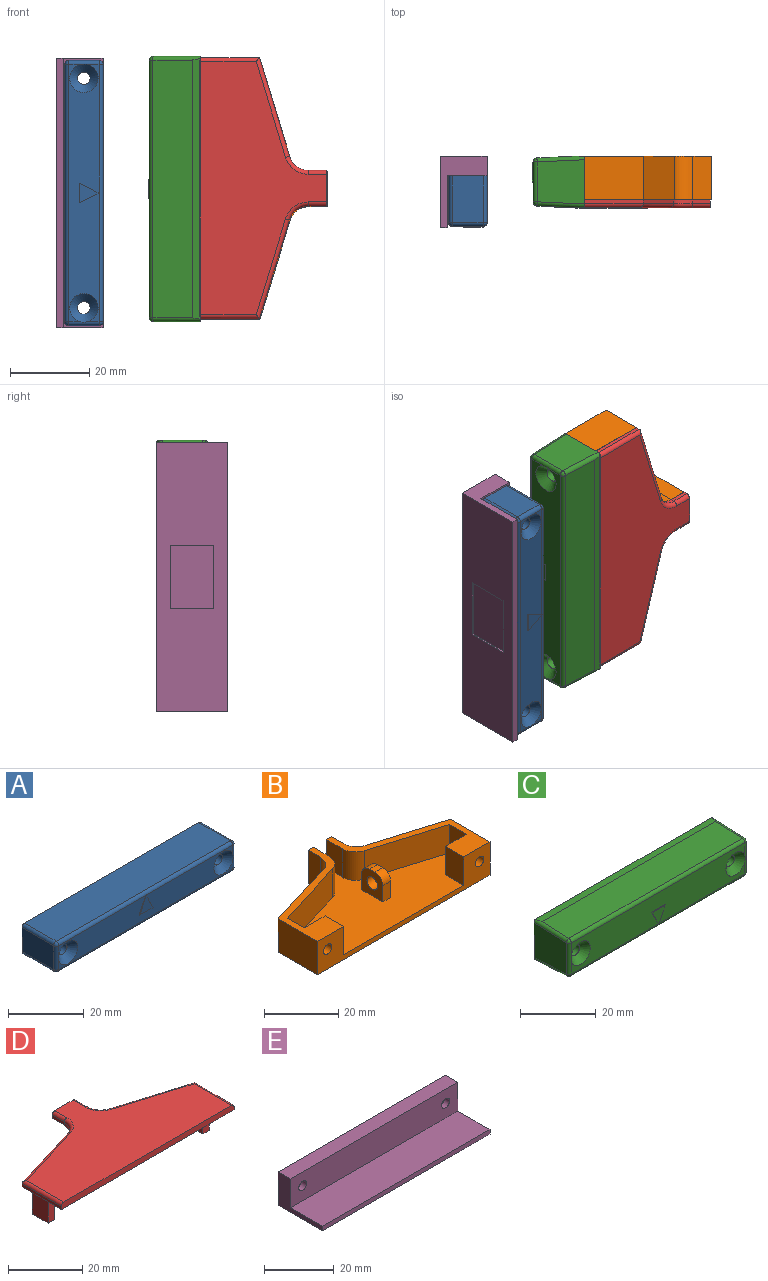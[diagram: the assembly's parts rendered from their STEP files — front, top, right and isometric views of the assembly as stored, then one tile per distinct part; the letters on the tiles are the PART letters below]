
ASSEMBLY  parts=5 mates=4
PART A: 26 faces, bbox 67x12.9x9.7 mm
  f0: plane 65x11.7mm, normal (0,0,1), area 760.5mm2, adj f5,f16,f22,f25
  f1: plane 11.7x7.7mm, normal (-1,0,0), area 90.1mm2, adj f5,f19,f23,f25
  f2: plane 65x11.7mm, normal (0,0,-1), area 760.5mm2, adj f5,f14,f18,f19
  f3: plane 11.7x7.7mm, normal (1,0,0), area 90.1mm2, adj f5,f14,f16,f17
  f4: plane 65x7.7mm, normal (0,-1,0), area 406.8mm2, adj f6,f7,f8,f12,f13,f17,f18,f22
  f5: plane 67x9.7mm, normal (0,1,0), area 633mm2, adj f0,f1,f2,f3,f10,f11,f14,f16
  f6: plane 5x2.5mm, normal (0.89,0,0.45), area 1.1mm2, adj f4,f7,f8,f9
  f7: plane 5x2.5mm, normal (-0.89,0,0.45), area 1.1mm2, adj f4,f6,f8,f9
  f8: plane 5x0.2mm, normal (0,0,-1), area 1mm2, adj f4,f6,f7,f9
  f9: plane 5x5mm, normal (0,-1,0), area 12.5mm2, adj f6,f7,f8
  f10: cylinder r=1.6mm len=10.7mm, axis (0,-1,0), area 107.6mm2, adj f5,f12
  f11: cylinder r=1.6mm len=10.7mm, axis (0,-1,0), area 107.6mm2, adj f5,f13
  f12: cone r=1.6mm half-angle=45deg, axis (0,-1,0), area 46.2mm2, adj f4,f10,f23
  f13: cone r=1.6mm half-angle=45deg, axis (0,-1,0), area 46.2mm2, adj f4,f11,f17
  f14: cylinder r=1mm len=11.7mm, axis (0,-1,0), area 18.4mm2, adj f2,f3,f5,f15
  f15: sphere r=1mm, area 1.6mm2, adj f14,f17,f18
  f16: cylinder r=1mm len=11.7mm, axis (0,1,0), area 18.4mm2, adj f0,f3,f5,f20
  f17: cylinder r=1mm len=7.7mm, axis (0,0,-1), area 12mm2, adj f3,f4,f13,f15,f20
  f18: cylinder r=1mm len=65mm, axis (-1,0,0), area 102.1mm2, adj f2,f4,f15,f21
  f19: cylinder r=1mm len=11.7mm, axis (0,1,0), area 18.4mm2, adj f1,f2,f5,f21
  f20: sphere r=1mm, area 1.6mm2, adj f16,f17,f22
  f21: sphere r=1mm, area 1.6mm2, adj f18,f19,f23
  f22: cylinder r=1mm len=65mm, axis (1,0,0), area 102.1mm2, adj f0,f4,f20,f24
  f23: cylinder r=1mm len=7.7mm, axis (0,0,1), area 12mm2, adj f1,f4,f12,f21,f24
  f24: sphere r=1mm, area 1.6mm2, adj f22,f23,f25
  f25: cylinder r=1mm len=11.7mm, axis (0,-1,0), area 18.4mm2, adj f0,f1,f5,f24
PART B: 57 faces, bbox 66x32x11 mm
  f0: plane 66x32mm, normal (0,0,-1), area 995.4mm2, adj f3,f4,f5,f6,f7,f8,f9,f10
  f1: plane 62x32mm, normal (0,0,1), area 1046.9mm2, adj f2,f4,f8,f11,f12,f14,f32,f33
  f2: plane 9.4x8mm, normal (0,1,0), area 48.1mm2, adj f1,f14,f15,f26,f27,f28,f29,f31
  f3: plane 15x11mm, normal (1,0,0), area 165mm2, adj f0,f4,f10,f15
  f4: plane 66x11mm, normal (0,-1,0), area 277.5mm2, adj f0,f1,f3,f5,f12,f13,f14,f15
  f5: plane 15x11mm, normal (-1,0,0), area 165mm2, adj f0,f4,f6,f13
  f6: plane 24.96x11mm, normal (-0.29,0.96,0), area 286.9mm2, adj f0,f5,f13,f50
  f7: plane 11x4.62mm, normal (-1,0,0), area 50.8mm2, adj f0,f8,f13,f50
  f8: plane 11x9mm, normal (0,1,0), area 52mm2, adj f0,f1,f7,f9,f13,f15,f34,f39
  f9: plane 11x4.62mm, normal (1,0,0), area 50.8mm2, adj f0,f8,f15,f51
  f10: plane 24.96x11mm, normal (0.29,0.96,0), area 286.9mm2, adj f0,f3,f15,f51
  f11: plane 9.4x8mm, normal (0,1,0), area 48.1mm2, adj f1,f12,f13,f19,f20,f21,f22,f23
  f12: plane 9.4x7mm, normal (1,0,0), area 65.8mm2, adj f1,f4,f11,f13
  f13: plane 32x30.5mm, normal (0,0,1), area 162.2mm2, adj f4,f5,f6,f7,f8,f11,f12,f32
  f14: plane 9.4x7mm, normal (-1,0,0), area 65.8mm2, adj f1,f2,f4,f15
  f15: plane 32x30.5mm, normal (0,0,1), area 162.2mm2, adj f2,f3,f4,f8,f9,f10,f14,f36
  f16: cylinder r=1.6mm len=3.2mm, axis (0,-1,0), area 30.2mm2, adj f4,f25
  f17: cylinder r=1.6mm len=3.2mm, axis (0,-1,0), area 30.2mm2, adj f4,f18
  f18: plane 6.93x6mm, normal (0,1,0), area 23.1mm2, adj f17,f19,f20,f21,f22,f23,f24
  f19: plane 4x3mm, normal (-0.5,0,-0.87), area 13.9mm2, adj f11,f18,f20,f22
  f20: plane 4x3.46mm, normal (-1,0,0), area 13.9mm2, adj f11,f18,f19,f21
  f21: plane 4x3mm, normal (-0.5,0,0.87), area 13.9mm2, adj f11,f18,f20,f23
  f22: plane 4x3mm, normal (0.5,0,-0.87), area 13.9mm2, adj f11,f18,f19,f24,f35
  f23: plane 4x3mm, normal (0.5,0,0.87), area 13.9mm2, adj f11,f18,f21,f24,f35
  f24: plane 4x3.46mm, normal (1,0,0), area 13.9mm2, adj f18,f22,f23,f35
  f25: plane 6.93x6mm, normal (0,1,0), area 23.1mm2, adj f16,f26,f27,f28,f29,f30,f31
  f26: plane 4x3mm, normal (0.5,0,0.87), area 13.9mm2, adj f2,f25,f27,f31
  f27: plane 4x3.46mm, normal (1,0,0), area 13.9mm2, adj f2,f25,f26,f28
  f28: plane 4x3mm, normal (0.5,0,-0.87), area 13.9mm2, adj f2,f25,f27,f29
  f29: plane 4x3mm, normal (-0.5,0,-0.87), area 13.9mm2, adj f2,f25,f28,f30,f38
  f30: plane 4x3.46mm, normal (-1,0,0), area 13.9mm2, adj f25,f29,f31,f38
  f31: plane 4x3mm, normal (-0.5,0,0.87), area 13.9mm2, adj f2,f25,f26,f30,f38
  f32: plane 9.4x6.52mm, normal (1,0,0), area 61.3mm2, adj f1,f11,f13,f33,f35
  f33: plane 24.96x9.4mm, normal (0.29,-0.96,0), area 245.2mm2, adj f1,f13,f32,f49
  f34: plane 9.4x6.1mm, normal (1,0,0), area 57.4mm2, adj f1,f8,f13,f49
  f35: plane 4.62x1mm, normal (0,-1,0), area 4mm2, adj f22,f23,f24,f32
  f36: plane 24.96x9.4mm, normal (-0.29,-0.96,0), area 245.2mm2, adj f1,f15,f37,f48
  f37: plane 9.4x6.52mm, normal (-1,0,0), area 61.3mm2, adj f1,f2,f15,f36,f38
  f38: plane 4.62x1mm, normal (0,-1,0), area 4mm2, adj f29,f30,f31,f37
  f39: plane 9.4x6.1mm, normal (-1,0,0), area 57.4mm2, adj f1,f8,f15,f48
  f40: plane 3x2mm, normal (0,0,1), area 6mm2, adj f41,f44,f46,f47
  f41: plane 8.4x8mm, normal (-1,0,0), area 50.8mm2, adj f1,f40,f42,f43,f45,f46,f47
  f42: plane 5.4x3mm, normal (0,-1,0), area 16.2mm2, adj f1,f41,f44,f46
  f43: plane 5.4x3mm, normal (0,1,0), area 16.2mm2, adj f1,f41,f44,f47
  f44: plane 8.4x8mm, normal (1,0,0), area 50.8mm2, adj f1,f40,f42,f43,f45,f46,f47
  f45: cylinder r=2mm len=4mm, axis (1,0,0), area 37.7mm2, adj f41,f44
  f46: cylinder r=3mm len=3mm, axis (-1,0,0), area 14.1mm2, adj f40,f41,f42,f44
  f47: cylinder r=3mm len=3mm, axis (1,0,0), area 14.1mm2, adj f40,f41,f43,f44
  f48: cylinder r=5mm len=9.4mm, axis (0,0,-1), area 59.9mm2, adj f1,f15,f36,f39
  f49: cylinder r=5mm len=9.4mm, axis (0,0,-1), area 59.9mm2, adj f1,f13,f33,f34
  f50: cylinder r=5mm len=11mm, axis (0,0,1), area 70.1mm2, adj f0,f6,f7,f13
  f51: cylinder r=5mm len=11mm, axis (0,0,1), area 70.1mm2, adj f0,f9,f10,f15
  f52: plane 25x0.4mm, normal (0,1,0), area 10mm2, adj f0,f53,f55,f56
  f53: plane 16x0.4mm, normal (1,0,0), area 6.4mm2, adj f0,f52,f54,f56
  f54: plane 25x0.4mm, normal (0,-1,0), area 10mm2, adj f0,f53,f55,f56
  f55: plane 16x0.4mm, normal (-1,0,0), area 6.4mm2, adj f0,f52,f54,f56
  f56: plane 25x16mm, normal (0,0,-1), area 400mm2, adj f52,f53,f54,f55
PART C: 28 faces, bbox 67x13.2x13.2 mm
  f0: plane 65x10.09mm, normal (0,-1,0), area 562.1mm2, adj f8,f9,f10,f14,f15,f19,f20,f24
  f1: plane 67.01x13.01mm, normal (0,1,0), area 854.3mm2, adj f2,f3,f4,f5,f12,f13,f16,f18
  f2: plane 65.83x2mm, normal (0,0,1), area 131.1mm2, adj f1,f6,f18,f27
  f3: plane 12x11.18mm, normal (-1,0,0), area 127.6mm2, adj f1,f21,f25,f27
  f4: plane 65.83x2mm, normal (0,0,-1), area 131.1mm2, adj f1,f7,f16,f21
  f5: plane 12x11.18mm, normal (1,0,0), area 127.6mm2, adj f1,f16,f18,f19
  f6: plane 65x10.05mm, normal (0,-0.05,1), area 653.6mm2, adj f2,f18,f24,f27
  f7: plane 65x10.05mm, normal (0,-0.05,-1), area 653.6mm2, adj f4,f16,f20,f21
  f8: plane 5x0.2mm, normal (0,0,1), area 1mm2, adj f0,f9,f10,f11
  f9: plane 5x2.5mm, normal (-0.89,0,-0.45), area 1.1mm2, adj f0,f8,f10,f11
  f10: plane 5x2.5mm, normal (0.89,0,-0.45), area 1.1mm2, adj f0,f8,f9,f11
  f11: plane 5x5mm, normal (0,-1,0), area 12.5mm2, adj f8,f9,f10
  f12: cylinder r=1.6mm len=11mm, axis (0,-1,0), area 110.6mm2, adj f1,f14
  f13: cylinder r=1.6mm len=11mm, axis (0,-1,0), area 110.6mm2, adj f1,f15
  f14: cone r=3.6mm half-angle=45deg, axis (0,-1,0), area 46.2mm2, adj f0,f12,f19
  f15: cone r=1.6mm half-angle=45deg, axis (0,-1,0), area 46.2mm2, adj f0,f13,f25
  f16: cylinder r=1mm len=12.09mm, axis (0,1,-0.05), area 18.3mm2, adj f1,f4,f5,f7,f17
  f17: sphere r=1mm, area 1.5mm2, adj f16,f19,f20
  f18: cylinder r=1mm len=12.09mm, axis (0,-1,-0.05), area 18.3mm2, adj f1,f2,f5,f6,f22
  f19: cylinder r=1mm len=10.09mm, axis (0,0,-1), area 15.7mm2, adj f0,f5,f14,f17,f22
  f20: cylinder r=1mm len=65mm, axis (-1,0,0), area 99.1mm2, adj f0,f7,f17,f23
  f21: cylinder r=1mm len=12.09mm, axis (0,1,-0.05), area 18.3mm2, adj f1,f3,f4,f7,f23
  f22: sphere r=1mm, area 1.5mm2, adj f18,f19,f24
  f23: sphere r=1mm, area 1.5mm2, adj f20,f21,f25
  f24: cylinder r=1mm len=65mm, axis (1,0,0), area 99.1mm2, adj f0,f6,f22,f26
  f25: cylinder r=1mm len=10.09mm, axis (0,0,1), area 15.7mm2, adj f0,f3,f15,f23,f26
  f26: sphere r=1mm, area 1.5mm2, adj f24,f25,f27
  f27: cylinder r=1mm len=12.09mm, axis (0,-1,-0.05), area 18.3mm2, adj f1,f2,f3,f6,f26
PART D: 30 faces, bbox 66x32x11.2 mm
  f0: plane 64x32mm, normal (0,0,1), area 1291.4mm2, adj f5,f10,f22,f23,f24,f25,f26,f27
  f1: plane 4.62x1mm, normal (-1,0,0), area 4.6mm2, adj f2,f8,f10,f23
  f2: cylinder r=5mm len=4.78mm, axis (0,0,-1), area 6.4mm2, adj f1,f3,f8,f25
  f3: plane 24.96x7.6mm, normal (-0.29,0.96,0), area 26.1mm2, adj f2,f4,f8,f24
  f4: plane 15x1mm, normal (-1,0,0), area 15mm2, adj f3,f5,f8,f22
  f5: plane 66x2mm, normal (0,-1,0), area 131.6mm2, adj f0,f4,f6,f8,f22,f26
  f6: plane 15x1mm, normal (1,0,0), area 15mm2, adj f5,f7,f8,f26
  f7: plane 24.96x7.6mm, normal (0.29,0.96,0), area 26.1mm2, adj f6,f8,f9,f28
  f8: plane 66x32mm, normal (0,0,-1), area 1365.4mm2, adj f1,f2,f3,f4,f5,f6,f7,f9
  f9: cylinder r=5mm len=4.78mm, axis (0,0,-1), area 6.4mm2, adj f7,f8,f11,f29
  f10: plane 9x2mm, normal (0,1,0), area 17.6mm2, adj f0,f1,f8,f11,f23,f27
  f11: plane 4.62x1mm, normal (1,0,0), area 4.6mm2, adj f8,f9,f10,f27
  f12: plane 6x2.5mm, normal (0,0,-1), area 15mm2, adj f13,f14,f15,f16
  f13: plane 9.2x6mm, normal (-1,0,0), area 55.2mm2, adj f8,f12,f14,f15
  f14: plane 9.2x2.5mm, normal (0,1,0), area 23mm2, adj f8,f12,f13,f16
  f15: plane 9.2x2.5mm, normal (0,-1,0), area 23mm2, adj f8,f12,f13,f16
  f16: plane 9.2x6mm, normal (1,0,0), area 55.2mm2, adj f8,f12,f14,f15
  f17: plane 6x2.5mm, normal (0,0,-1), area 15mm2, adj f18,f19,f20,f21
  f18: plane 9.2x2.5mm, normal (0,1,0), area 23mm2, adj f8,f17,f19,f21
  f19: plane 9.2x6mm, normal (1,0,0), area 55.2mm2, adj f8,f17,f18,f20
  f20: plane 9.2x2.5mm, normal (0,-1,0), area 23mm2, adj f8,f17,f19,f21
  f21: plane 9.2x6mm, normal (-1,0,0), area 55.2mm2, adj f8,f17,f18,f20
  f22: cylinder r=1mm len=15mm, axis (0,1,0), area 23.1mm2, adj f0,f4,f5,f24
  f23: cylinder r=1mm len=4.62mm, axis (0,1,0), area 7.3mm2, adj f0,f1,f10,f25
  f24: cylinder r=1mm len=25.25mm, axis (0.96,0.29,0), area 40.6mm2, adj f0,f3,f22,f25
  f25: torus R=6mm, axis (0,0,1), area 10.7mm2, adj f0,f2,f23,f24
  f26: cylinder r=1mm len=15mm, axis (0,-1,0), area 23.1mm2, adj f0,f5,f6,f28
  f27: cylinder r=1mm len=4.62mm, axis (0,-1,0), area 7.3mm2, adj f0,f10,f11,f29
  f28: cylinder r=1mm len=25.25mm, axis (0.96,-0.29,0), area 40.6mm2, adj f0,f7,f26,f29
  f29: torus R=6mm, axis (0,0,1), area 10.7mm2, adj f0,f9,f27,f28
PART E: 29 faces, bbox 68x18x11.7 mm
  f0: plane 68x18mm, normal (0,0,-1), area 1048mm2, adj f3,f4,f6,f9,f24,f25,f26,f27
  f1: cylinder r=1.6mm len=3.2mm, axis (0,-1,0), area 20.1mm2, adj f7,f17
  f2: cylinder r=1.6mm len=3.2mm, axis (0,-1,0), area 20.1mm2, adj f7,f10
  f3: plane 68x11.7mm, normal (0,1,0), area 733.2mm2, adj f0,f4,f5,f6,f11,f12,f13,f14
  f4: plane 18x11.7mm, normal (-1,0,0), area 79.3mm2, adj f0,f3,f5,f7,f8,f9
  f5: plane 68x5mm, normal (0,0,1), area 340mm2, adj f3,f4,f6,f7
  f6: plane 18x11.7mm, normal (1,0,0), area 79.3mm2, adj f0,f3,f5,f7,f8,f9
  f7: plane 68x10.1mm, normal (0,-1,0), area 670.7mm2, adj f1,f2,f4,f5,f6,f8
  f8: plane 68x13mm, normal (0,0,1), area 884mm2, adj f4,f6,f7,f9
  f9: plane 68x1.6mm, normal (0,-1,0), area 108.8mm2, adj f0,f4,f6,f8
  f10: plane 6.93x6mm, normal (0,1,0), area 23.1mm2, adj f2,f11,f12,f13,f14,f15,f16
  f11: plane 3x3mm, normal (0.5,0,-0.87), area 10.4mm2, adj f3,f10,f12,f14
  f12: plane 3x3mm, normal (-0.5,0,-0.87), area 10.4mm2, adj f3,f10,f11,f13
  f13: plane 3.46x3mm, normal (-1,0,0), area 10.4mm2, adj f3,f10,f12,f15
  f14: plane 3.46x3mm, normal (1,0,0), area 10.4mm2, adj f3,f10,f11,f16
  f15: plane 3x3mm, normal (-0.5,0,0.87), area 10.4mm2, adj f3,f10,f13,f16
  f16: plane 3x3mm, normal (0.5,0,0.87), area 10.4mm2, adj f3,f10,f14,f15
  f17: plane 6.93x6mm, normal (0,1,0), area 23.1mm2, adj f1,f18,f19,f20,f21,f22,f23
  f18: plane 3x3mm, normal (-0.5,0,0.87), area 10.4mm2, adj f3,f17,f19,f23
  f19: plane 3x3mm, normal (0.5,0,0.87), area 10.4mm2, adj f3,f17,f18,f20
  f20: plane 3.46x3mm, normal (1,0,0), area 10.4mm2, adj f3,f17,f19,f21
  f21: plane 3x3mm, normal (0.5,0,-0.87), area 10.4mm2, adj f3,f17,f20,f22
  f22: plane 3x3mm, normal (-0.5,0,-0.87), area 10.4mm2, adj f3,f17,f21,f23
  f23: plane 3.46x3mm, normal (-1,0,0), area 10.4mm2, adj f3,f17,f18,f22
  f24: plane 16x0.4mm, normal (0,1,0), area 6.4mm2, adj f0,f25,f27,f28
  f25: plane 11x0.4mm, normal (1,0,0), area 4.4mm2, adj f0,f24,f26,f28
  f26: plane 16x0.4mm, normal (0,-1,0), area 6.4mm2, adj f0,f25,f27,f28
  f27: plane 11x0.4mm, normal (-1,0,0), area 4.4mm2, adj f0,f24,f26,f28
  f28: plane 16x11mm, normal (0,0,-1), area 176mm2, adj f24,f25,f26,f27
PLACE A rot(axis=(0,1,0),90deg) t=(-38.9,15.87,64.44)mm
PLACE B rot(axis=(0.58,0.58,-0.58),120deg) t=(-25.75,14.37,65.49)mm fixed
PLACE C rot(axis=(0.58,0.58,-0.58),120deg) t=(-25.75,14.37,65.49)mm
PLACE D rot(axis=(0.58,0.58,-0.58),120deg) t=(-25.95,14.37,65.69)mm
PLACE E rot(axis=(0,1,0),90deg) t=(-38.9,15.87,64.44)mm
MATE fastened B.f17 <-> C.f13  axis (-1,0,0) through (-25.75,14.37,94.49)mm
MATE fastened E.f2 <-> A.f10  axis (0,-1,0) through (-55.25,15.87,93.44)mm
MATE planar B.f0 <-> E.f3  axis (0,1,0) through (-14.53,20.87,65.49)mm
MATE fastened B.f13 <-> D.f8  axis (0,-1,0) through (-18.75,9.87,96.49)mm
